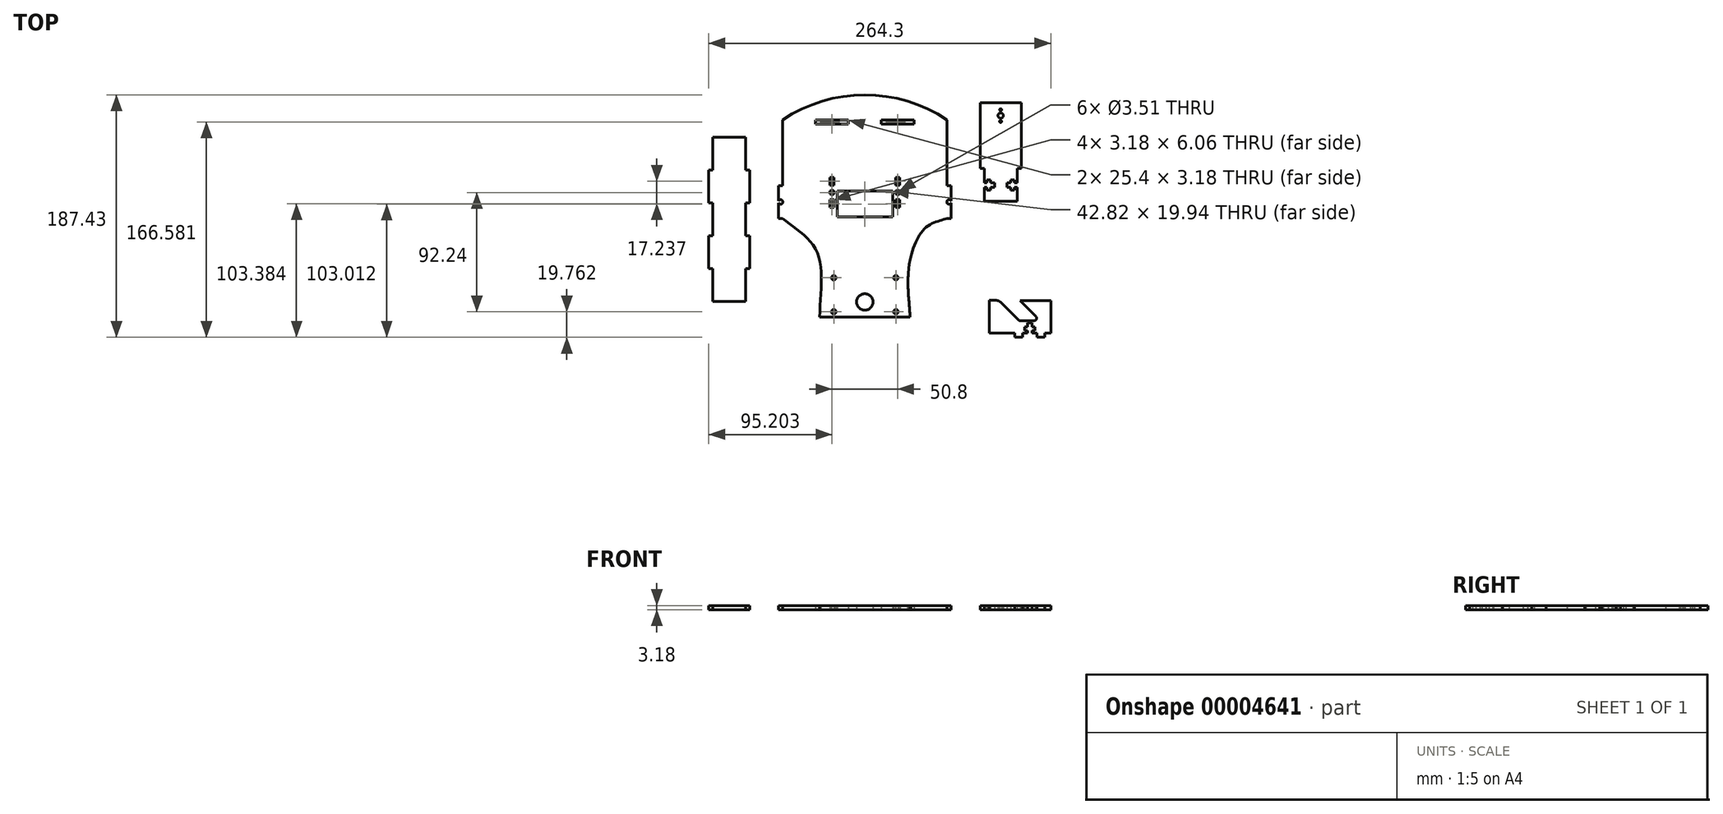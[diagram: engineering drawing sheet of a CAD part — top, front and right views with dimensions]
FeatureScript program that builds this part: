
annotation { "Feature Type Name" : "Feature", "Feature Type Description" : "" }
export const myFeature = defineFeature(function(context is Context, id is Id, definition is map)
    precondition{}
    {
        {
            var Q0;
            Q0=qCreatedBy(makeId("Top.planeOp"),FACE);
            var sketch = newSketch(context, id + "F0", { "sketchPlane" : qUnion([Q0])});
            skLineSegment(sketch, "E0", {"start": v(-1.69, -61.63) * mm, "end": v(33.24, -61.63) * mm});
            skLineSegment(sketch, "E1", {"start": v(61.81, 14.57) * mm, "end": v(61.81, 14.57) * mm});
            skPoint(sketch, "E2", {"position": v(-1.69, -61.63) * mm});
            skLineSegment(sketch, "E3.0.MirrorCS", {"start": v(-1.69, -61.63) * mm, "end": v(-36.61, -61.63) * mm});
            skPoint(sketch, "E4", {"position": v(-65.19, 14.57) * mm});
            skPoint(sketch, "E5.orphan", {"position": v(-65.19, -61.63) * mm});
            skFitSpline(sketch, "E6.0.MirrorCS", {"points": [v(61.81, 14.57) * mm, v(45.03, 7.13) * mm, v(32.1, -26.14) * mm, v(33.24, -61.63) * mm], "startDerivative": vector(-52.15, -19.53) * mm, "endDerivative": vector(3.8, -90.46) * mm});
            skPoint(sketch, "E7.orphan", {"position": v(61.81, -61.63) * mm});
            skLineSegment(sketch, "E8.trimOffspring", {"start": v(61.81, 39.97) * mm, "end": v(61.81, 90.77) * mm});
            skLineSegment(sketch, "E9", {"start": v(-73.21, 90.77) * mm, "end": v(111.84, 90.77) * mm, "construction": true});
            skLineSegment(sketch, "E10", {"start": v(-39.79, 90.77) * mm, "end": v(-39.79, 87.6) * mm});
            skLineSegment(sketch, "E11", {"start": v(-14.39, 87.6) * mm, "end": v(-14.39, 90.77) * mm});
            skLineSegment(sketch, "E12", {"start": v(-14.39, 90.77) * mm, "end": v(-39.79, 90.77) * mm});
            skLineSegment(sketch, "E13.0.MirrorCS", {"start": v(11.01, 87.6) * mm, "end": v(11.01, 90.77) * mm});
            skLineSegment(sketch, "E14.0.MirrorCS", {"start": v(11.01, 90.77) * mm, "end": v(36.41, 90.77) * mm});
            skLineSegment(sketch, "E15.0.MirrorCS", {"start": v(36.41, 90.77) * mm, "end": v(36.41, 87.6) * mm});
            skLineSegment(sketch, "E16.0.MirrorCS", {"start": v(36.41, 87.6) * mm, "end": v(11.01, 87.6) * mm});
            skLineSegment(sketch, "E17", {"start": v(27.76, -58.08) * mm, "end": v(27.76, -58.08) * mm});
            skFitSpline(sketch, "E18.0", {"points": [v(60.47, 18.16) * mm, v(60.01, 17.99) * mm, v(58.98, 17.64) * mm, v(56.56, 16.91) * mm, v(53.7, 16.08) * mm, v(50.63, 14.94) * mm, v(48.25, 13.89) * mm, v(45.85, 12.57) * mm, v(43.9, 11.2) * mm, v(42.37, 9.9) * mm, v(40.91, 8.5) * mm, v(39.24, 6.59) * mm, v(37.42, 4.04) * mm, v(35.8, 1.28) * mm, v(34.33, -1.66) * mm, v(32.6, -5.78) * mm, v(30.82, -11.24) * mm, v(29.52, -16.93) * mm, v(28.76, -21.53) * mm, v(28.34, -24.96) * mm, v(28.05, -28.35) * mm, v(27.84, -32.8) * mm, v(27.85, -38.19) * mm, v(28.16, -44.43) * mm, v(28.78, -52.44) * mm, v(29.25, -58.13) * mm, v(29.4, -61.8) * mm]});
            skFitSpline(sketch, "E19", {"points": [v(-36.61, -61.63) * mm, v(-39.02, -10.55) * mm, v(-65.19, 14.57) * mm], "startDerivative": vector(2.41, 101.96) * mm, "endDerivative": vector(-57.03, 48.48) * mm});
            skFitSpline(sketch, "E20.0.MirrorCS", {"points": [v(33.24, -61.63) * mm, v(35.64, -10.55) * mm, v(61.81, 14.57) * mm], "startDerivative": vector(-2.41, 101.96) * mm, "endDerivative": vector(57.03, 48.48) * mm});
            skLineSegment(sketch, "E21.trimOffspring", {"start": v(33.24, -61.63) * mm, "end": v(33.24, -61.63) * mm});
            skLineSegment(sketch, "E22", {"start": v(-36.16, -57.63) * mm, "end": v(-36.16, -57.63) * mm});
            skLineSegment(sketch, "E23", {"start": v(61.81, 39.97) * mm, "end": v(64.99, 39.97) * mm});
            skLineSegment(sketch, "E24", {"start": v(64.99, 14.57) * mm, "end": v(61.81, 14.57) * mm});
            skLineSegment(sketch, "E25.0.MirrorCS", {"start": v(-65.19, 39.97) * mm, "end": v(-68.36, 39.97) * mm});
            skLineSegment(sketch, "E26.0.MirrorCS", {"start": v(-68.36, 39.97) * mm, "end": v(-68.36, 28.01) * mm});
            skLineSegment(sketch, "E27.0.MirrorCS", {"start": v(-68.36, 14.57) * mm, "end": v(-65.19, 14.57) * mm});
            skLineSegment(sketch, "E28.0.MirrorCS", {"start": v(-65.19, 39.97) * mm, "end": v(-65.19, 90.77) * mm});
            skLineSegment(sketch, "E29.0.MirrorCS", {"start": v(-65.19, 14.57) * mm, "end": v(-65.19, 14.57) * mm});
            skPoint(sketch, "E30", {"position": v(-1.69, -29.88) * mm});
            skPoint(sketch, "E31", {"position": v(-33.44, -61.63) * mm});
            skLineSegment(sketch, "E32.bottom", {"start": v(-33.44, -61.63) * mm, "end": v(-1.2, -99.6) * mm, "construction": true});
            skLineSegment(sketch, "E33", {"start": v(-33.44, -61.63) * mm, "end": v(-13.25, -44.49) * mm, "construction": true});
            skLineSegment(sketch, "E34.0.MirrorCS", {"start": v(30.06, -61.63) * mm, "end": v(-10.32, -27.34) * mm, "construction": true});
            skLineSegment(sketch, "E35", {"start": v(-10.32, -27.34) * mm, "end": v(6.95, -27.34) * mm, "construction": true});
            skCircle(sketch, "E36", {"center": v(-25.69, -57.64) * mm, "radius": 1.75 * mm});
            skLineSegment(sketch, "E37", {"start": v(-13.25, -44.49) * mm, "end": v(67.28, -44.49) * mm, "construction": true});
            skLineSegment(sketch, "E38", {"start": v(-25.69, -57.64) * mm, "end": v(-30.39, -61.63) * mm, "construction": true});
            skLineSegment(sketch, "E39", {"start": v(-25.69, -57.64) * mm, "end": v(-28.73, -57.64) * mm, "construction": true});
            skCircle(sketch, "E40.0.MirrorC", {"center": v(22.31, -57.64) * mm, "radius": 1.75 * mm});
            skCircle(sketch, "E41.0.MirrorC", {"center": v(-25.69, -31.34) * mm, "radius": 1.75 * mm});
            skCircle(sketch, "E42.0.MirrorC", {"center": v(22.31, -31.34) * mm, "radius": 1.75 * mm});
            skLineSegment(sketch, "E43", {"start": v(-25.69, -31.34) * mm, "end": v(-25.69, -29.58) * mm, "construction": true});
            skLineSegment(sketch, "E44", {"start": v(-25.69, -31.34) * mm, "end": v(-27.44, -31.34) * mm, "construction": true});
            skPoint(sketch, "E45", {"position": v(-27.09, 22.95) * mm});
            skLineSegment(sketch, "E46", {"start": v(-27.09, 22.95) * mm, "end": v(-25.5, 22.95) * mm});
            skLineSegment(sketch, "E47.0.MirrorCS", {"start": v(-27.09, 22.95) * mm, "end": v(-28.67, 22.95) * mm});
            skLineSegment(sketch, "E48", {"start": v(-28.67, 22.95) * mm, "end": v(-28.67, 29.01) * mm});
            skLineSegment(sketch, "E49", {"start": v(-28.67, 29.01) * mm, "end": v(-25.5, 29.01) * mm});
            skLineSegment(sketch, "E50", {"start": v(-25.5, 29.01) * mm, "end": v(-25.5, 22.95) * mm});
            skLineSegment(sketch, "E51.1.MirrorCS", {"start": v(25.3, 22.95) * mm, "end": v(25.3, 29.01) * mm});
            skLineSegment(sketch, "E51.2.MirrorCS", {"start": v(22.13, 29.01) * mm, "end": v(22.13, 22.95) * mm});
            skLineSegment(sketch, "E51.3.MirrorCS", {"start": v(23.71, 22.95) * mm, "end": v(22.13, 22.95) * mm});
            skPoint(sketch, "E51.5.MirrorP", {"position": v(23.71, 22.95) * mm});
            skLineSegment(sketch, "E51.6.MirrorCS", {"start": v(23.71, 22.95) * mm, "end": v(25.3, 22.95) * mm});
            skLineSegment(sketch, "E51.7.MirrorCS", {"start": v(25.3, 29.01) * mm, "end": v(22.13, 29.01) * mm});
            skCircle(sketch, "E52", {"center": v(-1.69, -50.05) * mm, "radius": 6.35 * mm});
            skLineSegment(sketch, "E53", {"start": v(64.99, 39.97) * mm, "end": v(64.99, 28.01) * mm});
            skArc(sketch, "E54", {"start": v(64.99, 28.01) * mm, "mid": v(61.65, 27.27) * mm, "end": v(64.99, 26.53) * mm});
            skLineSegment(sketch, "E55.trimOffspring", {"start": v(64.99, 26.53) * mm, "end": v(64.99, 14.57) * mm});
            skArc(sketch, "E56.0.MirrorCS", {"start": v(-68.36, 28.01) * mm, "mid": v(-65.02, 27.27) * mm, "end": v(-68.36, 26.53) * mm});
            skLineSegment(sketch, "E57.trimOffspring", {"start": v(-68.36, 26.53) * mm, "end": v(-68.36, 14.57) * mm});
            skLineSegment(sketch, "E58", {"start": v(-39.79, 87.6) * mm, "end": v(-14.39, 87.6) * mm});
            skArc(sketch, "E59", {"start": v(61.81, 90.77) * mm, "mid": v(-1.69, 110.03) * mm, "end": v(-65.19, 90.77) * mm});
            skCircle(sketch, "E60.0.MirrorC", {"center": v(-27.09, 34.6) * mm, "radius": 1.75 * mm});
            skCircle(sketch, "E61.0.MirrorC", {"center": v(23.71, 34.6) * mm, "radius": 1.75 * mm});
            skLineSegment(sketch, "E62.0.MirrorCS", {"start": v(22.13, 46.25) * mm, "end": v(22.13, 40.2) * mm});
            skLineSegment(sketch, "E63.0.MirrorCS", {"start": v(25.3, 40.2) * mm, "end": v(25.3, 46.25) * mm});
            skLineSegment(sketch, "E64.0.MirrorCS", {"start": v(23.71, 40.2) * mm, "end": v(22.13, 40.2) * mm});
            skLineSegment(sketch, "E65.0.MirrorCS", {"start": v(23.71, 40.2) * mm, "end": v(25.3, 40.2) * mm});
            skLineSegment(sketch, "E66.0.MirrorCS", {"start": v(25.3, 46.25) * mm, "end": v(22.13, 46.25) * mm});
            skLineSegment(sketch, "E67.0.MirrorCS", {"start": v(-28.67, 46.25) * mm, "end": v(-25.5, 46.25) * mm});
            skLineSegment(sketch, "E68.0.MirrorCS", {"start": v(-25.5, 46.25) * mm, "end": v(-25.5, 40.2) * mm});
            skLineSegment(sketch, "E69.0.MirrorCS", {"start": v(-28.67, 40.2) * mm, "end": v(-28.67, 46.25) * mm});
            skLineSegment(sketch, "E70.0.MirrorCS", {"start": v(-27.09, 40.2) * mm, "end": v(-25.5, 40.2) * mm});
            skLineSegment(sketch, "E71.0.MirrorCS", {"start": v(-27.09, 40.2) * mm, "end": v(-28.67, 40.2) * mm});
            skPoint(sketch, "E72.start.orphan", {"position": v(25.3, 25.98) * mm});
            skLineSegment(sketch, "E73", {"start": v(22.13, 25.98) * mm, "end": v(-25.5, 25.98) * mm, "construction": true});
            skPoint(sketch, "E74", {"position": v(-1.69, 25.98) * mm});
            skLineSegment(sketch, "E75.1", {"start": v(-23.1, 18.57) * mm, "end": v(-23.1, 15.64) * mm});
            skLineSegment(sketch, "E75.2", {"start": v(-23.1, 18.57) * mm, "end": v(-23.1, 35.58) * mm});
            skLineSegment(sketch, "E75.3", {"start": v(-23.1, 35.58) * mm, "end": v(19.72, 35.58) * mm});
            skLineSegment(sketch, "E75.4", {"start": v(19.72, 18.57) * mm, "end": v(19.72, 35.58) * mm});
            skLineSegment(sketch, "E75.5", {"start": v(19.72, 18.57) * mm, "end": v(19.72, 15.64) * mm});
            skPoint(sketch, "E76.rect.right.end.orphan", {"position": v(17.54, 33.4) * mm});
            skPoint(sketch, "E77.start.orphan", {"position": v(17.54, 18.57) * mm});
            skPoint(sketch, "E78.orphan", {"position": v(-20.91, 18.57) * mm});
            skPoint(sketch, "E76.rect.left.end.orphan", {"position": v(-20.91, 33.4) * mm});
            skLineSegment(sketch, "E79", {"start": v(-23.1, 15.64) * mm, "end": v(19.72, 15.64) * mm});
            skPoint(sketch, "E75.0.end.orphan", {"position": v(19.72, 12.71) * mm});
            skPoint(sketch, "E80.orphan", {"position": v(-23.1, 12.71) * mm});
            skSolve(sketch);
        }
        {
            var Q0;
            Q0=makeQuery(id+"F0.imprint","IMPRINT",FACE,{"disambiguationData":[TD([[makeQuery(id+"F0.imprint","IMPRINT",EDGE,{"derivedFrom":sQuery(id+"F0.wireOp",EDGE,"E3.0.MirrorCS")}),-1.0]])]});
            extrude(context, id + "F1", {"entities" : qUnion([Q0]), "depth" : 3.17 * mm});
        }
        {
            var Q0;
            Q0=qCreatedBy(makeId("Top.planeOp"),FACE);
            var sketch = newSketch(context, id + "F2", { "sketchPlane" : qUnion([Q0])});
            skLineSegment(sketch, "E81", {"start": v(87.38, 103.96) * mm, "end": v(87.38, 53.16) * mm});
            skPoint(sketch, "E82", {"position": v(87.38, 53.16) * mm});
            skPoint(sketch, "E83", {"position": v(87.38, 27.76) * mm});
            skLineSegment(sketch, "E84", {"start": v(87.38, 53.16) * mm, "end": v(90.56, 53.16) * mm});
            skLineSegment(sketch, "E85", {"start": v(90.56, 53.16) * mm, "end": v(90.56, 42.22) * mm});
            skLineSegment(sketch, "E86", {"start": v(90.56, 42.22) * mm, "end": v(92.59, 42.22) * mm});
            skLineSegment(sketch, "E87.0.MirrorCS", {"start": v(90.56, 38.71) * mm, "end": v(92.59, 38.71) * mm});
            skLineSegment(sketch, "E88.trimOffspring", {"start": v(90.56, 38.71) * mm, "end": v(90.56, 27.76) * mm});
            skLineSegment(sketch, "E89", {"start": v(92.59, 42.22) * mm, "end": v(92.59, 44.43) * mm});
            skLineSegment(sketch, "E90", {"start": v(92.59, 44.43) * mm, "end": v(95.37, 44.43) * mm});
            skLineSegment(sketch, "E91", {"start": v(95.37, 44.43) * mm, "end": v(95.37, 42.22) * mm});
            skLineSegment(sketch, "E92.0.MirrorCS", {"start": v(92.59, 36.5) * mm, "end": v(95.37, 36.5) * mm});
            skLineSegment(sketch, "E93.trimOffspring", {"start": v(95.37, 42.22) * mm, "end": v(98.5, 42.22) * mm});
            skLineSegment(sketch, "E94", {"start": v(98.5, 42.22) * mm, "end": v(98.5, 38.71) * mm});
            skLineSegment(sketch, "E95", {"start": v(98.5, 38.71) * mm, "end": v(95.37, 38.71) * mm});
            skLineSegment(sketch, "E96", {"start": v(95.37, 38.71) * mm, "end": v(95.37, 36.5) * mm});
            skPoint(sketch, "E97.orphan", {"position": v(112.88, 42.22) * mm});
            skPoint(sketch, "E98.orphan", {"position": v(112.88, 38.71) * mm});
            skLineSegment(sketch, "E99", {"start": v(92.59, 36.5) * mm, "end": v(92.59, 38.71) * mm});
            skLineSegment(sketch, "E100", {"start": v(92.59, 38.71) * mm, "end": v(90.56, 38.71) * mm});
            skLineSegment(sketch, "E101.trimOffspring", {"start": v(95.37, 38.71) * mm, "end": v(98.5, 38.71) * mm});
            skLineSegment(sketch, "E102", {"start": v(87.38, 103.96) * mm, "end": v(111.92, 103.96) * mm});
            skLineSegment(sketch, "E103.0.MirrorCS", {"start": v(115.96, 38.71) * mm, "end": v(113.93, 38.71) * mm});
            skLineSegment(sketch, "E103.1.MirrorCS", {"start": v(113.93, 38.71) * mm, "end": v(115.96, 38.71) * mm});
            skLineSegment(sketch, "E103.2.MirrorCS", {"start": v(111.15, 38.71) * mm, "end": v(111.15, 36.5) * mm});
            skLineSegment(sketch, "E103.3.MirrorCS", {"start": v(113.93, 36.5) * mm, "end": v(113.93, 38.71) * mm});
            skLineSegment(sketch, "E103.4.MirrorCS", {"start": v(119.13, 53.16) * mm, "end": v(115.96, 53.16) * mm});
            skLineSegment(sketch, "E103.5.MirrorCS", {"start": v(111.15, 44.43) * mm, "end": v(111.15, 42.22) * mm});
            skLineSegment(sketch, "E103.6.MirrorCS", {"start": v(113.93, 42.22) * mm, "end": v(113.93, 44.43) * mm});
            skLineSegment(sketch, "E103.7.MirrorCS", {"start": v(113.93, 44.43) * mm, "end": v(111.15, 44.43) * mm});
            skLineSegment(sketch, "E103.8.MirrorCS", {"start": v(113.93, 36.5) * mm, "end": v(111.15, 36.5) * mm});
            skLineSegment(sketch, "E103.10.MirrorCS", {"start": v(115.96, 42.22) * mm, "end": v(113.93, 42.22) * mm});
            skPoint(sketch, "E103.11.MirrorP", {"position": v(119.13, 27.76) * mm});
            skPoint(sketch, "E103.12.MirrorP", {"position": v(119.13, 53.16) * mm});
            skLineSegment(sketch, "E103.14.MirrorCS", {"start": v(115.96, 53.16) * mm, "end": v(115.96, 42.22) * mm});
            skLineSegment(sketch, "E103.15.MirrorCS", {"start": v(119.13, 103.96) * mm, "end": v(94.6, 103.96) * mm});
            skLineSegment(sketch, "E103.16.MirrorCS", {"start": v(119.13, 103.96) * mm, "end": v(119.13, 53.16) * mm});
            skLineSegment(sketch, "E103.18.MirrorCS", {"start": v(115.96, 38.71) * mm, "end": v(115.96, 27.76) * mm});
            skLineSegment(sketch, "E104.0.MirrorCS", {"start": v(108, 42.22) * mm, "end": v(108, 38.71) * mm});
            skLineSegment(sketch, "E105.0.MirrorCS", {"start": v(111.15, 42.22) * mm, "end": v(108, 42.22) * mm});
            skLineSegment(sketch, "E106.0.MirrorCS", {"start": v(111.15, 38.71) * mm, "end": v(108, 38.71) * mm});
            skLineSegment(sketch, "E107.trimOffspring", {"start": v(98.5, 40.46) * mm, "end": v(96.63, 40.46) * mm, "construction": true});
            skPoint(sketch, "E108.start.orphan", {"position": v(108, 40.46) * mm});
            skPoint(sketch, "E109", {"position": v(103.26, 44.96) * mm});
            skLineSegment(sketch, "E110", {"start": v(103.26, 40.46) * mm, "end": v(92.44, 40.46) * mm, "construction": true});
            skLineSegment(sketch, "E111", {"start": v(90.56, 27.76) * mm, "end": v(115.96, 27.76) * mm});
            skLineSegment(sketch, "E112", {"start": v(103.26, 40.46) * mm, "end": v(103.26, 45.76) * mm, "construction": true});
            skCircle(sketch, "E113.0.MirrorC", {"center": v(103.26, 94.06) * mm, "radius": 2.05 * mm});
            skCircle(sketch, "E114.0.MirrorC", {"center": v(103.26, 98.56) * mm, "radius": 0.8 * mm});
            skPoint(sketch, "E115.0.MirrorP", {"position": v(103.26, 89.56) * mm});
            skCircle(sketch, "E116.0.MirrorC", {"center": v(103.26, 89.56) * mm, "radius": 0.8 * mm});
            skSolve(sketch);
        }
        {
            var Q0;
            Q0=makeQuery(id+"F2.imprint","IMPRINT",FACE,{"disambiguationData":[TD([[makeQuery(id+"F2.imprint","IMPRINT",EDGE,{"derivedFrom":sQuery(id+"F2.wireOp",EDGE,"E81")}),1.0]])]});
            extrude(context, id + "F3", {"entities" : qUnion([Q0]), "depth" : 3.17 * mm});
        }
        {
            var Q0;
            Q0=qCreatedBy(makeId("Top.planeOp"),FACE);
            var sketch = newSketch(context, id + "F4", { "sketchPlane" : qUnion([Q0])});
            skLineSegment(sketch, "E117", {"start": v(-93.72, 77.34) * mm, "end": v(-93.72, 51.94) * mm});
            skLineSegment(sketch, "E118", {"start": v(-93.72, 77.34) * mm, "end": v(-119.12, 77.34) * mm});
            skPoint(sketch, "E119", {"position": v(-93.72, 13.84) * mm});
            skPoint(sketch, "E120", {"position": v(-93.72, 26.54) * mm});
            skLineSegment(sketch, "E121", {"start": v(-93.72, 26.54) * mm, "end": v(-90.54, 26.54) * mm});
            skLineSegment(sketch, "E122", {"start": v(-90.54, 26.54) * mm, "end": v(-90.54, 51.94) * mm});
            skLineSegment(sketch, "E123", {"start": v(-90.54, 51.94) * mm, "end": v(-93.72, 51.94) * mm});
            skLineSegment(sketch, "E124.trimOffspring", {"start": v(-93.72, 26.54) * mm, "end": v(-93.72, 1.14) * mm});
            skLineSegment(sketch, "E125", {"start": v(-93.72, 13.84) * mm, "end": v(-119.12, 13.84) * mm, "construction": true});
            skLineSegment(sketch, "E126", {"start": v(-106.42, 77.34) * mm, "end": v(-106.42, 13.84) * mm, "construction": true});
            skLineSegment(sketch, "E127.0.MirrorCS", {"start": v(-119.12, 77.34) * mm, "end": v(-119.12, 51.94) * mm});
            skLineSegment(sketch, "E128.0.MirrorCS", {"start": v(-122.3, 26.54) * mm, "end": v(-122.3, 51.94) * mm});
            skLineSegment(sketch, "E129.0.MirrorCS", {"start": v(-122.3, 51.94) * mm, "end": v(-119.12, 51.94) * mm});
            skLineSegment(sketch, "E130.0.MirrorCS", {"start": v(-119.12, 26.54) * mm, "end": v(-122.3, 26.54) * mm});
            skLineSegment(sketch, "E131.0.MirrorCS", {"start": v(-119.12, 26.54) * mm, "end": v(-119.12, 1.14) * mm});
            skLineSegment(sketch, "E132.0.MirrorCS", {"start": v(-93.72, -49.66) * mm, "end": v(-119.12, -49.66) * mm});
            skLineSegment(sketch, "E133.0.MirrorCS", {"start": v(-90.54, 1.14) * mm, "end": v(-90.54, -24.26) * mm});
            skLineSegment(sketch, "E134.0.MirrorCS", {"start": v(-93.72, 1.14) * mm, "end": v(-90.54, 1.14) * mm});
            skLineSegment(sketch, "E135.0.MirrorCS", {"start": v(-90.54, -24.26) * mm, "end": v(-93.72, -24.26) * mm});
            skLineSegment(sketch, "E136.0.MirrorCS", {"start": v(-122.3, -24.26) * mm, "end": v(-119.12, -24.26) * mm});
            skLineSegment(sketch, "E137.0.MirrorCS", {"start": v(-119.12, 1.14) * mm, "end": v(-122.3, 1.14) * mm});
            skLineSegment(sketch, "E138.0.MirrorCS", {"start": v(-122.3, 1.14) * mm, "end": v(-122.3, -24.26) * mm});
            skLineSegment(sketch, "E139.trimOffspring", {"start": v(-93.72, -24.26) * mm, "end": v(-93.72, -49.66) * mm});
            skLineSegment(sketch, "E140.trimOffspring", {"start": v(-119.12, -24.26) * mm, "end": v(-119.12, -49.66) * mm});
            skSolve(sketch);
        }
        {
            var Q0;
            Q0=makeQuery(id+"F4.imprint","IMPRINT",FACE,{"disambiguationData":[TD([[makeQuery(id+"F4.imprint","IMPRINT",EDGE,{"derivedFrom":sQuery(id+"F4.wireOp",EDGE,"E117")}),-1.0]])]});
            extrude(context, id + "F5", {"entities" : qUnion([Q0]), "depth" : 3.17 * mm});
        }
        {
            var Q0;
            Q0=qCreatedBy(makeId("Top.planeOp"),FACE);
            var sketch = newSketch(context, id + "F6", { "sketchPlane" : qUnion([Q0])});
            skLineSegment(sketch, "E141", {"start": v(142.01, -48.91) * mm, "end": v(142.01, -74.22) * mm});
            skPoint(sketch, "E142", {"position": v(125.72, -74.22) * mm});
            skLineSegment(sketch, "E143", {"start": v(114.07, -74.22) * mm, "end": v(114.07, -77.4) * mm});
            skLineSegment(sketch, "E144", {"start": v(114.07, -77.4) * mm, "end": v(120.13, -77.4) * mm});
            skLineSegment(sketch, "E145", {"start": v(120.13, -77.4) * mm, "end": v(120.13, -74.22) * mm});
            skPoint(sketch, "E146", {"position": v(117.1, -77.4) * mm});
            skLineSegment(sketch, "E147", {"start": v(117.1, -77.4) * mm, "end": v(117.1, -72.67) * mm, "construction": true});
            skLineSegment(sketch, "E148", {"start": v(125.72, -74.22) * mm, "end": v(125.72, -47.49) * mm, "construction": true});
            skLineSegment(sketch, "E149.0.MirrorCS", {"start": v(131.3, -77.4) * mm, "end": v(131.3, -74.22) * mm});
            skLineSegment(sketch, "E150.0.MirrorCS", {"start": v(137.37, -77.4) * mm, "end": v(131.3, -77.4) * mm});
            skLineSegment(sketch, "E151.0.MirrorCS", {"start": v(137.37, -74.22) * mm, "end": v(137.37, -77.4) * mm});
            skLineSegment(sketch, "E152", {"start": v(123.97, -74.22) * mm, "end": v(123.97, -72.19) * mm});
            skLineSegment(sketch, "E153", {"start": v(123.97, -72.19) * mm, "end": v(121.75, -72.19) * mm});
            skLineSegment(sketch, "E154", {"start": v(121.75, -72.19) * mm, "end": v(121.75, -69.41) * mm});
            skLineSegment(sketch, "E155", {"start": v(121.75, -69.41) * mm, "end": v(123.97, -69.41) * mm});
            skLineSegment(sketch, "E156", {"start": v(123.97, -69.41) * mm, "end": v(123.97, -66.27) * mm});
            skLineSegment(sketch, "E157", {"start": v(123.97, -66.27) * mm, "end": v(125.72, -66.27) * mm});
            skLineSegment(sketch, "E158.0.MirrorCS", {"start": v(127.47, -66.27) * mm, "end": v(125.72, -66.27) * mm});
            skLineSegment(sketch, "E159.0.MirrorCS", {"start": v(127.47, -69.41) * mm, "end": v(127.47, -66.27) * mm});
            skLineSegment(sketch, "E160.0.MirrorCS", {"start": v(129.69, -69.41) * mm, "end": v(127.47, -69.41) * mm});
            skLineSegment(sketch, "E161.0.MirrorCS", {"start": v(129.69, -72.19) * mm, "end": v(129.69, -69.41) * mm});
            skLineSegment(sketch, "E162.0.MirrorCS", {"start": v(127.47, -72.19) * mm, "end": v(129.69, -72.19) * mm});
            skLineSegment(sketch, "E163.0.MirrorCS", {"start": v(127.47, -74.22) * mm, "end": v(127.47, -72.19) * mm});
            skLineSegment(sketch, "E164.trimOffspring", {"start": v(127.47, -74.22) * mm, "end": v(131.3, -74.22) * mm});
            skLineSegment(sketch, "E165.trimOffspring", {"start": v(120.13, -74.22) * mm, "end": v(123.97, -74.22) * mm});
            skLineSegment(sketch, "E166.trimOffspring", {"start": v(137.37, -74.22) * mm, "end": v(142.01, -74.22) * mm});
            skLineSegment(sketch, "E167", {"start": v(114.07, -74.22) * mm, "end": v(110.35, -74.22) * mm});
            skLineSegment(sketch, "E168.trimOffspring", {"start": v(142.01, -48.91) * mm, "end": v(142.63, -48.91) * mm});
            skLineSegment(sketch, "E169", {"start": v(110.35, -74.22) * mm, "end": v(106.28, -74.22) * mm});
            skLineSegment(sketch, "E170", {"start": v(130.34, -65.62) * mm, "end": v(84.75, -65.62) * mm, "construction": true});
            skLineSegment(sketch, "E171", {"start": v(106.28, -74.22) * mm, "end": v(94.62, -74.22) * mm});
            skLineSegment(sketch, "E172", {"start": v(94.62, -74.22) * mm, "end": v(94.62, -48.82) * mm});
            skLineSegment(sketch, "E173", {"start": v(94.62, -48.82) * mm, "end": v(98.47, -48.82) * mm});
            skLineSegment(sketch, "E174", {"start": v(110.41, -57.34) * mm, "end": v(103.75, -50.68) * mm});
            skLineSegment(sketch, "E175.trimOffspring", {"start": v(117.48, -64.42) * mm, "end": v(110.41, -57.34) * mm});
            skLineSegment(sketch, "E176", {"start": v(117.87, -64.57) * mm, "end": v(129.26, -64.49) * mm});
            skLineSegment(sketch, "E177", {"start": v(130.2, -48.91) * mm, "end": v(144.39, -48.91) * mm});
            skPoint(sketch, "E178.visualSharp", {"position": v(101.89, -48.82) * mm});
            skLineSegment(sketch, "E179", {"start": v(103.75, -50.68) * mm, "end": v(103.75, -50.68) * mm});
            skLineSegment(sketch, "E180", {"start": v(98.47, -48.82) * mm, "end": v(99.26, -48.82) * mm});
            skArc(sketch, "E181.filletArc", {"start": v(103.75, -50.68) * mm, "mid": v(101.69, -49.3) * mm, "end": v(99.26, -48.82) * mm});
            skLineSegment(sketch, "E182", {"start": v(130.2, -48.91) * mm, "end": v(120.95, -48.91) * mm});
            skPoint(sketch, "E183.visualSharp", {"position": v(117.64, -64.57) * mm});
            skArc(sketch, "E183.filletArc", {"start": v(117.48, -64.42) * mm, "mid": v(117.66, -64.53) * mm, "end": v(117.87, -64.57) * mm});
            skLineSegment(sketch, "E184.0", {"start": v(125.73, -56.5) * mm, "end": v(119.82, -50.59) * mm});
            skLineSegment(sketch, "E184.1", {"start": v(125.73, -56.5) * mm, "end": v(130.56, -61.32) * mm});
            skLineSegment(sketch, "E185", {"start": v(130.34, -64.48) * mm, "end": v(131.47, -64.47) * mm});
            skLineSegment(sketch, "E186", {"start": v(120.95, -48.91) * mm, "end": v(118.14, -48.91) * mm});
            skLineSegment(sketch, "E187", {"start": v(119.82, -50.59) * mm, "end": v(118.14, -48.91) * mm});
            skPoint(sketch, "E188.orphan", {"position": v(115.34, -48.91) * mm});
            skPoint(sketch, "E189.visualSharp", {"position": v(133.7, -64.46) * mm});
            skArc(sketch, "E189.filletArc", {"start": v(132.4, -64.47) * mm, "mid": v(132.9, -64.13) * mm, "end": v(132.78, -63.55) * mm});
            skArc(sketch, "E190.filletArc", {"start": v(131.47, -64.47) * mm, "mid": v(132.32, -63.9) * mm, "end": v(132.12, -62.89) * mm});
            skPoint(sketch, "E191.newPointA", {"position": v(130.34, -64.48) * mm});
            skArc(sketch, "E191.filletArc", {"start": v(129.26, -64.49) * mm, "mid": v(130.96, -63.33) * mm, "end": v(130.56, -61.32) * mm});
            skSolve(sketch);
        }
        {
            var Q0;
            Q0=makeQuery(id+"F6.imprint","IMPRINT",FACE,{"disambiguationData":[TD([[makeQuery(id+"F6.imprint","IMPRINT",EDGE,{"derivedFrom":sQuery(id+"F6.wireOp",EDGE,"E141")}),-1.0]])]});
            extrude(context, id + "F7", {"entities" : qUnion([Q0]), "depth" : 3.17 * mm});
        }
    });
